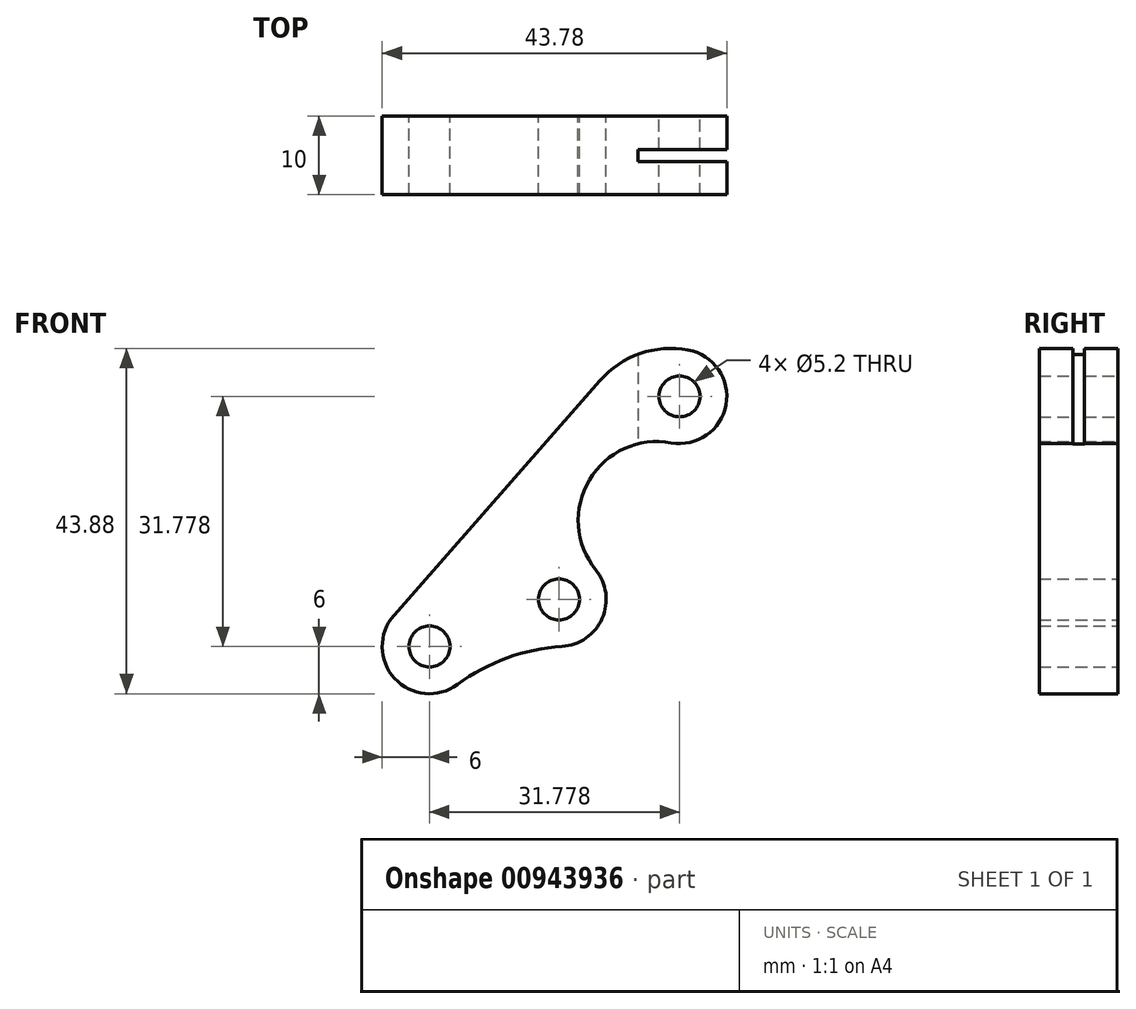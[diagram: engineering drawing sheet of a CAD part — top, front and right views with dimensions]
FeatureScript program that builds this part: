
annotation { "Feature Type Name" : "Feature", "Feature Type Description" : "" }
export const myFeature = defineFeature(function(context is Context, id is Id, definition is map)
    precondition{}
    {
        {
            var Q0;
            Q0=qCreatedBy(makeId("Front.planeOp"),FACE);
            var sketch = newSketch(context, id + "F0", { "sketchPlane" : qUnion([Q0])});
            skLineSegment(sketch, "E0", {"start": v(-4.5, 3.96) * mm, "end": v(21.68, 33.8) * mm});
            skArc(sketch, "E1", {"start": v(-4.5, 3.96) * mm, "mid": v(-4.42, -4.06) * mm, "end": v(3.56, -4.83) * mm});
            skCircle(sketch, "E2", {"center": v(0, 0) * mm, "radius": 2.6 * mm});
            skArc(sketch, "E3", {"start": v(3.56, -4.83) * mm, "mid": v(9.85, -1.46) * mm, "end": v(16.83, 0) * mm});
            skArc(sketch, "E4", {"start": v(16.83, 0) * mm, "mid": v(21.94, 3.57) * mm, "end": v(21.12, 9.76) * mm});
            skCircle(sketch, "E5", {"center": v(16.45, 5.99) * mm, "radius": 2.6 * mm});
            skLineSegment(sketch, "E6", {"start": v(0, 0) * mm, "end": v(0, 54.68) * mm, "construction": true});
            skArc(sketch, "E7", {"start": v(21.68, 33.8) * mm, "mid": v(26.76, 37.2) * mm, "end": v(32.86, 37.68) * mm});
            skArc(sketch, "E8", {"start": v(32.86, 37.68) * mm, "mid": v(37.68, 30.7) * mm, "end": v(30.7, 25.88) * mm});
            skLineSegment(sketch, "E9", {"start": v(0, 0) * mm, "end": v(31.78, 31.78) * mm, "construction": true});
            skCircle(sketch, "E10", {"center": v(31.78, 31.78) * mm, "radius": 2.6 * mm});
            skArc(sketch, "E11", {"start": v(30.7, 25.88) * mm, "mid": v(20.3, 21.15) * mm, "end": v(21.12, 9.76) * mm});
            skLineSegment(sketch, "E12", {"start": v(0, 0) * mm, "end": v(16.45, 5.99) * mm, "construction": true});
            skLineSegment(sketch, "E13", {"start": v(16.45, 5.99) * mm, "end": v(31.78, 31.78) * mm, "construction": true});
            skSolve(sketch);
        }
        {
            var Q0;
            Q0=makeQuery(id+"F0.imprint","IMPRINT",FACE,{"disambiguationData":[TD([[makeQuery(id+"F0.imprint","IMPRINT",EDGE,{"derivedFrom":sQuery(id+"F0.wireOp",EDGE,"E0")}),-1.0]])]});
            extrude(context, id + "F1", {"entities" : qUnion([Q0]), "depth" : 5 * mm, "offsetDistance" : 25 * mm, "hasSecondDirection" : true, "secondDirectionOppositeDirection" : true, "secondDirectionDepth" : 5 * mm});
        }
        {
            var Q0;
            Q0=qCreatedBy(makeId("Top.planeOp"),FACE);
            var sketch = newSketch(context, id + "F2", { "sketchPlane" : qUnion([Q0])});
            skLineSegment(sketch, "E14.bottom", {"start": v(41.1, -0.75) * mm, "end": v(26.49, -0.75) * mm});
            skLineSegment(sketch, "E14.top", {"start": v(41.1, 0.75) * mm, "end": v(26.49, 0.75) * mm});
            skLineSegment(sketch, "E14.left", {"start": v(41.1, -0.75) * mm, "end": v(41.1, 0.75) * mm});
            skLineSegment(sketch, "E14.right", {"start": v(26.49, -0.75) * mm, "end": v(26.49, 0.75) * mm});
            skSolve(sketch);
        }
        {
            var Q0;
            Q0 = qSketchRegion(id + "F2", true);
            extrude(context, id + "F3", {"entities" : qUnion([Q0]), "operationType" : NewBodyOperationType.REMOVE, "depth" : 50 * mm, "offsetDistance" : 25 * mm});
        }
    });
